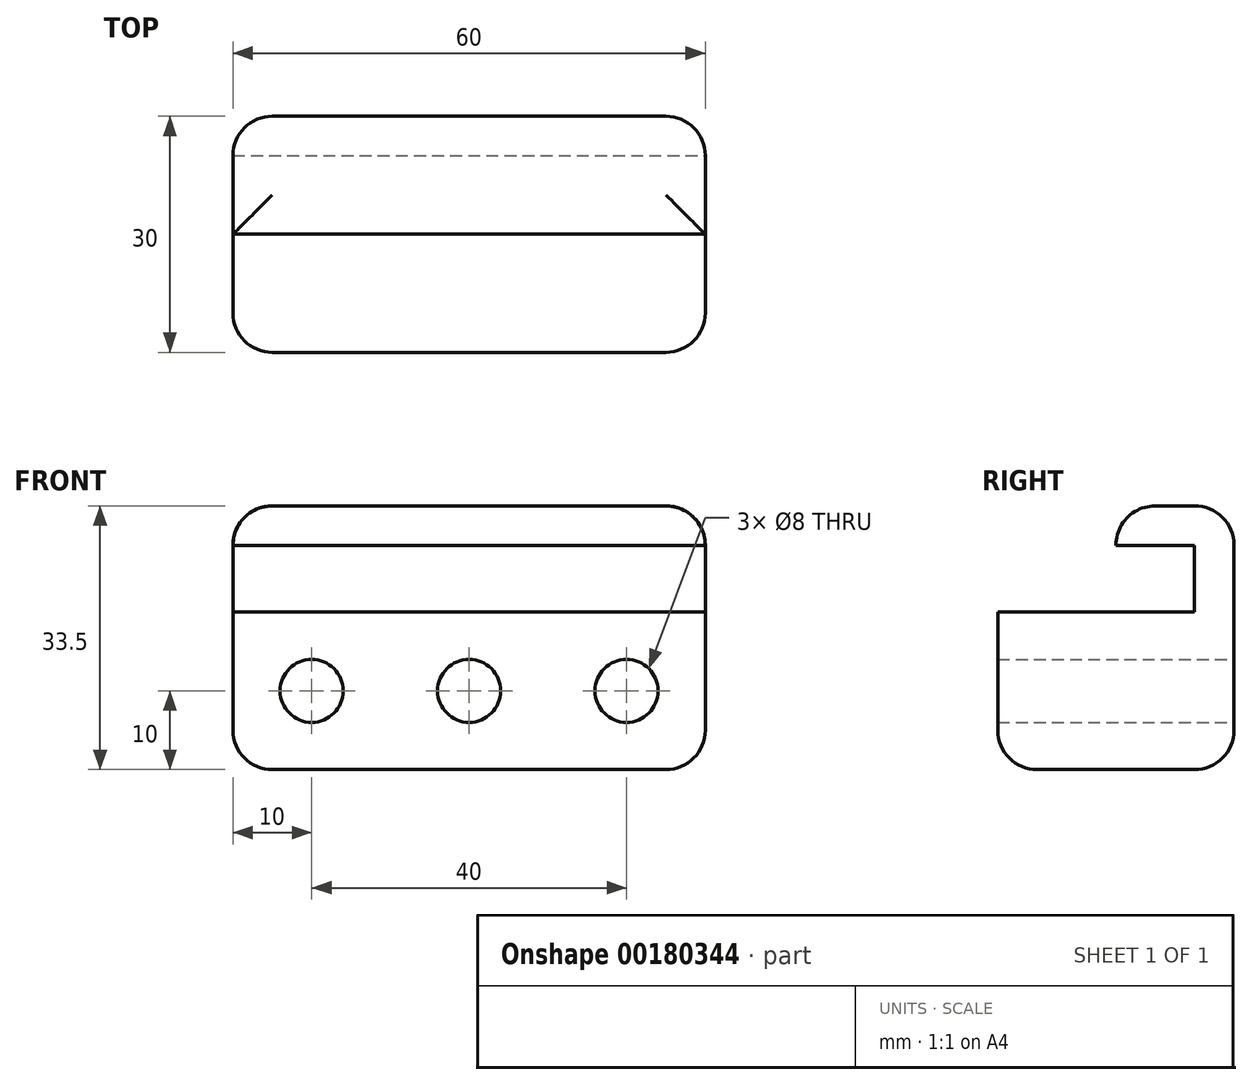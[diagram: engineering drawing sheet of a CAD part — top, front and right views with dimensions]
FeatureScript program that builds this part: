
annotation { "Feature Type Name" : "Feature", "Feature Type Description" : "" }
export const myFeature = defineFeature(function(context is Context, id is Id, definition is map)
    precondition{}
    {
        {
            var Q0;
            Q0=qCreatedBy(makeId("Front.planeOp"),FACE);
            var sketch = newSketch(context, id + "F0", { "sketchPlane" : qUnion([Q0])});
            skLineSegment(sketch, "E0.bottom", {"start": v(-30, -20) * mm, "end": v(30, -20) * mm});
            skLineSegment(sketch, "E0.top", {"start": v(-30, 0) * mm, "end": v(30, 0) * mm});
            skLineSegment(sketch, "E0.left", {"start": v(-30, -20) * mm, "end": v(-30, 0) * mm});
            skLineSegment(sketch, "E0.right", {"start": v(30, -20) * mm, "end": v(30, 0) * mm});
            skSolve(sketch);
        }
        {
            var Q0;
            Q0 = qSketchRegion(id + "F0", true);
            extrude(context, id + "F1", {"entities" : qUnion([Q0]), "offsetDistance" : 25 * mm, "depth" : 30 * mm});
        }
        {
            var Q0;
            Q0=qCreatedBy(makeId("Front.planeOp"),FACE);
            var sketch = newSketch(context, id + "F2", { "sketchPlane" : qUnion([Q0])});
            skLineSegment(sketch, "E1.bottom", {"start": v(-30, 0) * mm, "end": v(30, 0) * mm});
            skLineSegment(sketch, "E1.top", {"start": v(-30, 8.5) * mm, "end": v(30, 8.5) * mm});
            skLineSegment(sketch, "E1.left", {"start": v(-30, 0) * mm, "end": v(-30, 8.5) * mm});
            skLineSegment(sketch, "E1.right", {"start": v(30, 0) * mm, "end": v(30, 8.5) * mm});
            skSolve(sketch);
        }
        {
            var Q0;
            Q0 = qSketchRegion(id + "F2", true);
            extrude(context, id + "F3", {"entities" : qUnion([Q0]), "operationType" : NewBodyOperationType.ADD, "offsetDistance" : 25 * mm, "depth" : 5 * mm});
        }
        {
            var Q0;
            Q0=qCreatedBy(makeId("Front.planeOp"),FACE);
            var sketch = newSketch(context, id + "F4", { "sketchPlane" : qUnion([Q0])});
            skLineSegment(sketch, "E2.bottom", {"start": v(-30, 8.5) * mm, "end": v(30, 8.5) * mm});
            skLineSegment(sketch, "E2.top", {"start": v(-30, 13.5) * mm, "end": v(30, 13.5) * mm});
            skLineSegment(sketch, "E2.left", {"start": v(-30, 8.5) * mm, "end": v(-30, 13.5) * mm});
            skLineSegment(sketch, "E2.right", {"start": v(30, 8.5) * mm, "end": v(30, 13.5) * mm});
            skSolve(sketch);
        }
        {
            var Q0;
            Q0 = qSketchRegion(id + "F4", true);
            extrude(context, id + "F5", {"entities" : qUnion([Q0]), "operationType" : NewBodyOperationType.ADD, "depth" : 15 * mm});
        }
        {
            var Q0;
            Q0=qCreatedBy(makeId("Front.planeOp"),FACE);
            var sketch = newSketch(context, id + "F6", { "sketchPlane" : qUnion([Q0])});
            skCircle(sketch, "E3", {"center": v(-20, -10) * mm, "radius": 4 * mm});
            skPoint(sketch, "E4", {"position": v(-19.97, -6) * mm});
            skCircle(sketch, "E5.1.0.0", {"center": v(0, -10) * mm, "radius": 4 * mm});
            skCircle(sketch, "E5.2.0.0", {"center": v(20, -10) * mm, "radius": 4 * mm});
            skLineSegment(sketch, "E5.direction1", {"start": v(-20, -10) * mm, "end": v(0, -10) * mm, "construction": true});
            skSolve(sketch);
        }
        {
            var Q0;
            Q0 = qSketchRegion(id + "F6", true);
            extrude(context, id + "F7", {"entities" : qUnion([Q0]), "operationType" : NewBodyOperationType.REMOVE, "endBound" : BoundingType.THROUGH_ALL, "depth" : 25 * mm});
        }
        {
            var Q0;
            Q0=makeQuery(id+"F1.opExtrude","SWEPT_EDGE",EDGE,{"disambiguationData":[OSD([sQuery(id+"F0.wireOp",EDGE,"E0.bottom"),sQuery(id+"F0.wireOp",EDGE,"E0.right")])]});
            var Q1;
            Q1=makeQuery(id+"F1.opExtrude","CAP_EDGE",EDGE,{"disambiguationData":[OSD([sQuery(id+"F0.wireOp",EDGE,"E0.right")])],"isStart":false});
            var Q2;
            Q2=makeQuery(id+"F5.opExtrude","SWEPT_EDGE",EDGE,{"disambiguationData":[OSD([sQuery(id+"F4.wireOp",EDGE,"E2.top"),sQuery(id+"F4.wireOp",EDGE,"E2.right")])]});
            var Q3;
            Q3=makeQuery(id+"F5.opExtrude","CAP_EDGE",EDGE,{"disambiguationData":[OSD([sQuery(id+"F4.wireOp",EDGE,"E2.top")])],"isStart":true});
            var Q4;
            Q4=makeQuery(id+"F1.opExtrude","CAP_EDGE",EDGE,{"disambiguationData":[OSD([sQuery(id+"F0.wireOp",EDGE,"E0.bottom")])],"isStart":true});
            var Q5;
            Q5=makeQuery(id+"F1.opExtrude","SWEPT_FACE",FACE,{"disambiguationData":[OSD([sQuery(id+"F0.wireOp",EDGE,"E0.bottom")])]});
            var Q6;
            Q6=makeQuery(id+"F1.opExtrude","CAP_EDGE",EDGE,{"disambiguationData":[OSD([sQuery(id+"F0.wireOp",EDGE,"E0.left")])],"isStart":false});
            var Q7;
            Q7=makeQuery(id+"F5.opExtrude","SWEPT_EDGE",EDGE,{"disambiguationData":[OSD([sQuery(id+"F4.wireOp",EDGE,"E2.top"),sQuery(id+"F4.wireOp",EDGE,"E2.left")])]});
            var Q8;
            Q8=makeQuery(id+"F5.boolean.opBoolean","MERGE",EDGE,{"derivedFrom":[makeQuery(id+"F3.boolean.opBoolean","MERGE",EDGE,{"derivedFrom":[makeQuery(id+"F1.opExtrude","CAP_EDGE",EDGE,{"disambiguationData":[OSD([sQuery(id+"F0.wireOp",EDGE,"E0.left")])],"isStart":true}),makeQuery(id+"F3.opExtrude","CAP_EDGE",EDGE,{"disambiguationData":[OSD([sQuery(id+"F2.wireOp",EDGE,"E1.left")])],"isStart":true})]}),makeQuery(id+"F5.opExtrude","CAP_EDGE",EDGE,{"disambiguationData":[OSD([sQuery(id+"F4.wireOp",EDGE,"E2.left")])],"isStart":true})]});
            var Q9;
            Q9=makeQuery(id+"F5.opExtrude","CAP_EDGE",EDGE,{"disambiguationData":[OSD([sQuery(id+"F4.wireOp",EDGE,"E2.top")])],"isStart":false});
            var Q10;
            Q10=makeQuery(id+"F5.boolean.opBoolean","MERGE",EDGE,{"derivedFrom":[makeQuery(id+"F3.boolean.opBoolean","MERGE",EDGE,{"derivedFrom":[makeQuery(id+"F1.opExtrude","CAP_EDGE",EDGE,{"disambiguationData":[OSD([sQuery(id+"F0.wireOp",EDGE,"E0.right")])],"isStart":true}),makeQuery(id+"F3.opExtrude","CAP_EDGE",EDGE,{"disambiguationData":[OSD([sQuery(id+"F2.wireOp",EDGE,"E1.right")])],"isStart":true})]}),makeQuery(id+"F5.opExtrude","CAP_EDGE",EDGE,{"disambiguationData":[OSD([sQuery(id+"F4.wireOp",EDGE,"E2.right")])],"isStart":true})]});
            fillet(context, id + "F8", {"entities" : qUnion([Q0, Q1, Q2, Q3, Q4, Q5, Q6, Q7, Q8, Q9, Q10]), "radius" : 5 * mm, "tangentPropagation" : true, "allowEdgeOverflow" : false});
        }
    });
